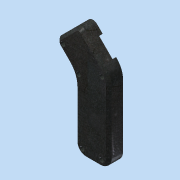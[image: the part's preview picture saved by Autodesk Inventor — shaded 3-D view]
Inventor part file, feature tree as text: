
AUTODESK INVENTOR PART (.ipt)
format: ipt  version: 2015 (Build 190159000, 159)  size: 221,184 bytes
history: native  units: in
note: dims shown in document units (in); Inventor stores cm internally (conversion verified against a paired STEP export)
features: other x3, sketch x3, extrude x2
ambient origin geometry x8: Origin, YZ Plane, XZ Plane, XY Plane, X Axis, Y Axis, Z Axis, Center Point
bodies: Solid1 (feature_tree)
feature tree (8):
  other  "CaseRight.ipt"
  extrude  "Extrusion1"  Depth=0.125in TaperAngle=0.0deg
  extrude  "Extrusion2"  Depth=0.0312in TaperAngle=0.0deg
  other  "Solid1::CaseRight.ipt"
  other  "TaggingFeature1"
  sketch  "Sketch3"  dims[d4=0.0312in d5=0.0312in d6=0.0in]
  sketch  "Sketch2"  dims[d0=0.3937in d1=0.125in d2=0.0in]
  sketch  "Sketch4"
